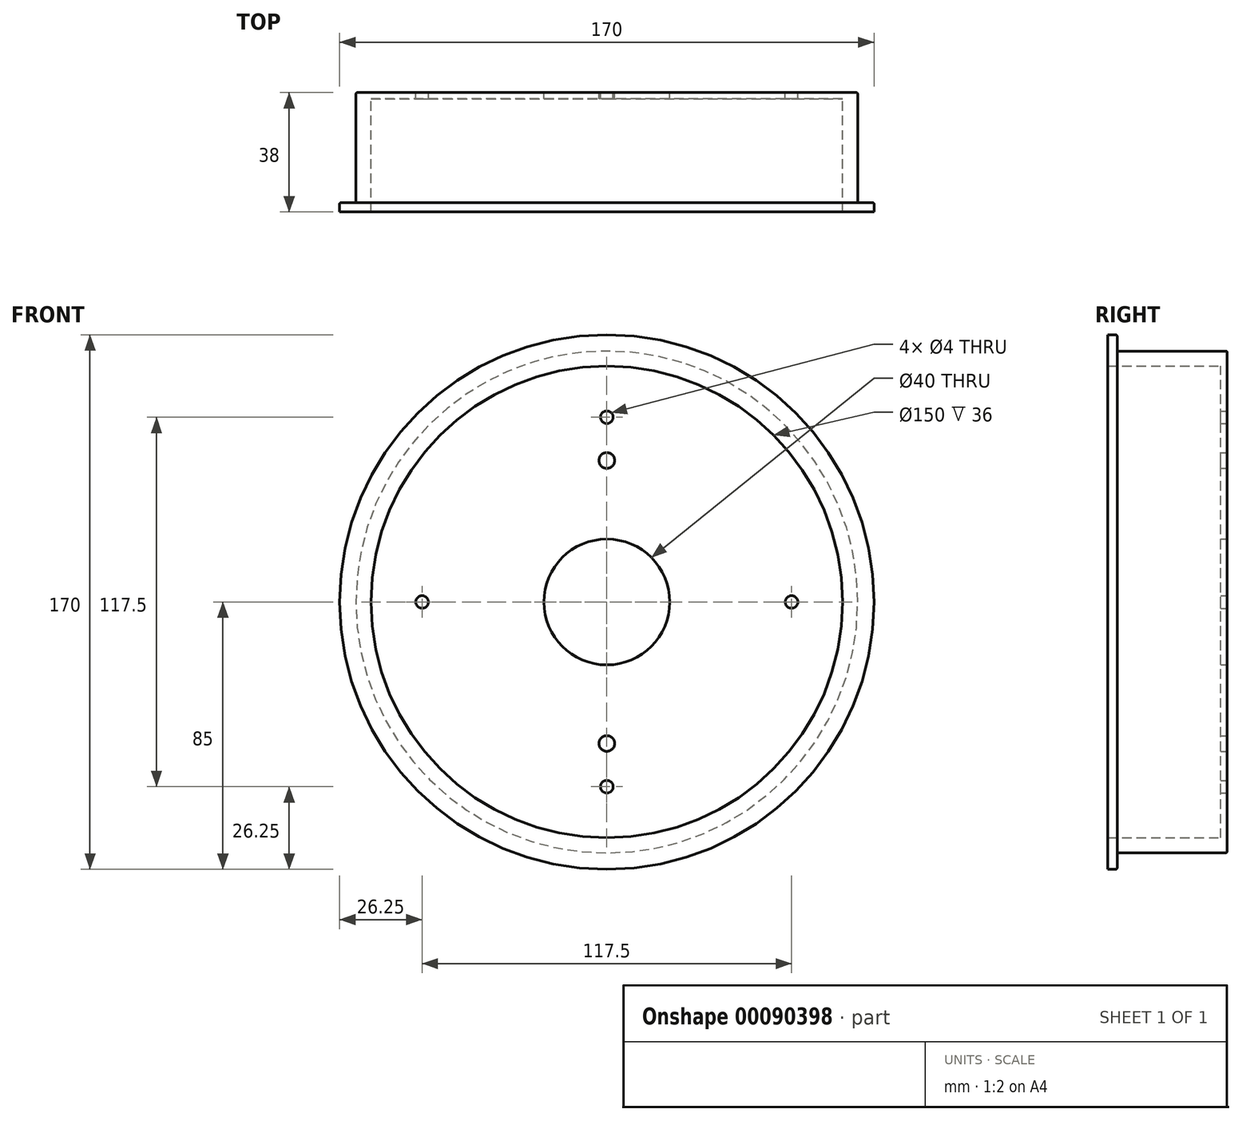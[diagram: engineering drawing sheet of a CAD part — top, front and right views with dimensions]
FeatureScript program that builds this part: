
annotation { "Feature Type Name" : "Feature", "Feature Type Description" : "" }
export const myFeature = defineFeature(function(context is Context, id is Id, definition is map)
    precondition{}
    {
        {
            var Q0;
            Q0=qCreatedBy(makeId("Front.planeOp"),FACE);
            var sketch = newSketch(context, id + "F0", { "sketchPlane" : qUnion([Q0])});
            skCircle(sketch, "E0", {"center": v(0, 0) * mm, "radius": 79.8 * mm});
            skCircle(sketch, "E1", {"center": v(0, 0) * mm, "radius": 20 * mm});
            skSolve(sketch);
        }
        {
            var Q0;
            Q0 = qSketchRegion(id + "F0", true);
            extrude(context, id + "F1", {"entities" : qUnion([Q0]), "depth" : 5 * mm});
        }
        {
            var Q0;
            Q0=makeQuery(id+"F1.opExtrude","CAP_FACE",FACE,{"disambiguationData":[OSD([sQuery(id+"F0.wireOp",EDGE,"E0"),sQuery(id+"F0.wireOp",EDGE,"E1")])],"isStart":false});
            var sketch = newSketch(context, id + "F2", { "sketchPlane" : qUnion([Q0])});
            skCircle(sketch, "E2", {"center": v(0, 0) * mm, "radius": 79.8 * mm});
            skCircle(sketch, "E3", {"center": v(0, 0) * mm, "radius": 75 * mm});
            skSolve(sketch);
        }
        {
            var Q0;
            Q0 = qSketchRegion(id + "F2", true);
            extrude(context, id + "F3", {"entities" : qUnion([Q0]), "operationType" : NewBodyOperationType.ADD, "depth" : 30 * mm});
        }
        {
            var Q0;
            Q0=makeQuery(id+"F3.opExtrude","CAP_FACE",FACE,{"disambiguationData":[OSD([sQuery(id+"F2.wireOp",EDGE,"E2"),sQuery(id+"F2.wireOp",EDGE,"E3")])],"isStart":false});
            var sketch = newSketch(context, id + "F4", { "sketchPlane" : qUnion([Q0])});
            skCircle(sketch, "E4", {"center": v(0, 0) * mm, "radius": 75 * mm});
            skCircle(sketch, "E5", {"center": v(0, 0) * mm, "radius": 85 * mm});
            skSolve(sketch);
        }
        {
            var Q0;
            Q0 = qSketchRegion(id + "F4", true);
            extrude(context, id + "F5", {"entities" : qUnion([Q0]), "operationType" : NewBodyOperationType.ADD, "depth" : 3 * mm});
        }
        {
            var Q0;
            {var subQ0=sQuery(id+"F0.wireOp",EDGE,"E1");Q0=makeQuery(id+"Fkw0NaJdu9EZw4x_1.boolean.opBoolean","SPLIT",FACE,{"disambiguationData":[TD([makeQuery(id+"F1.opExtrude","SWEPT_FACE",FACE,{"disambiguationData":[OSD([subQ0])]})])],"derivedFrom":makeQuery(id+"F1.opExtrude","CAP_FACE",FACE,{"disambiguationData":[OSD([sQuery(id+"F0.wireOp",EDGE,"E0"),subQ0])],"isStart":true})});}
            var sketch = newSketch(context, id + "F6", { "sketchPlane" : qUnion([Q0])});
            skCircle(sketch, "E6", {"center": v(0, 0) * mm, "radius": 45 * mm});
            skPoint(sketch, "E7", {"position": v(0, 45) * mm});
            skPoint(sketch, "E8", {"position": v(0, -45) * mm});
            skSolve(sketch);
        }
        {
            var Q0;
            Q0=sQuery(id+"F6.wireOp",VERTEX,"E7");
            var Q1;
            Q1=sQuery(id+"F6.wireOp",VERTEX,"E8");
            var Q2;
            Q2=makeQuery(id+"F1.opExtrude","SWEPT_BODY",BODY,{"disambiguationData":[OSD([sQuery(id+"F0.wireOp",EDGE,"E0"),sQuery(id+"F0.wireOp",EDGE,"E1")])]});
            hole(context, id + "F7", {"style" : HoleStyle.SIMPLE, "endStyle" : HoleEndStyle.BLIND, "holeDiameter" : 5 * mm, "holeDepth" : 25 * mm, "startFromSketch" : true, "locations" : qUnion([Q0, Q1]), "scope" : qUnion([Q2])});
        }
        {
            var Q0;
            Q0=makeQuery(id+"Fkw0NaJdu9EZw4x_1.opExtrude","CAP_FACE",FACE,{"disambiguationData":[OSD([sQuery(id+"FUGyWykdeStrJJa_1.wireOp",EDGE,"18ovhjpk-NtQe-Y3bV-f5br-2dgLtojzSKIQ"),sQuery(id+"FUGyWykdeStrJJa_1.wireOp",EDGE,"Cdf01vxO-JlfB-BUwl-xnIF-D1IGmlszCuzn")])],"isStart":false});
            var Q1;
            Q1=makeQuery(id+"F1.opExtrude","CAP_EDGE",EDGE,{"disambiguationData":[OSD([sQuery(id+"F0.wireOp",EDGE,"E0")])],"isStart":true});
            var Q2;
            Q2=makeQuery(id+"F5.opExtrude","CAP_EDGE",EDGE,{"disambiguationData":[OSD([sQuery(id+"F4.wireOp",EDGE,"E5")])],"isStart":true});
            fillet(context, id + "F8", {"entities" : qUnion([Q0, Q1, Q2]), "radius" : 0.5 * mm, "tangentPropagation" : true, "allowEdgeOverflow" : false});
        }
        {
            var Q0;
            Q0=makeQuery(id+"F1.opExtrude","CAP_FACE",FACE,{"disambiguationData":[OSD([sQuery(id+"F0.wireOp",EDGE,"E0"),sQuery(id+"F0.wireOp",EDGE,"E1")])],"isStart":false});
            extrude(context, id + "F9", {"entities" : qUnion([Q0]), "operationType" : NewBodyOperationType.REMOVE, "oppositeDirection" : true, "depth" : 3 * mm});
        }
        {
            var Q0;
            Q0=makeQuery(id+"F1.opExtrude","CAP_FACE",FACE,{"disambiguationData":[OSD([sQuery(id+"F0.wireOp",EDGE,"E0"),sQuery(id+"F0.wireOp",EDGE,"E1")])],"isStart":true});
            var sketch = newSketch(context, id + "F10", { "sketchPlane" : qUnion([Q0])});
            skCircle(sketch, "E9", {"center": v(0, 0) * mm, "radius": 58.75 * mm});
            skPoint(sketch, "E10", {"position": v(-58.75, 0) * mm});
            skPoint(sketch, "E11", {"position": v(0, 58.75) * mm});
            skPoint(sketch, "E12", {"position": v(58.75, 0) * mm});
            skPoint(sketch, "E13", {"position": v(0, -58.75) * mm});
            skSolve(sketch);
        }
        {
            var Q0;
            Q0=sQuery(id+"F10.wireOp",VERTEX,"E10");
            var Q1;
            Q1=sQuery(id+"F10.wireOp",VERTEX,"E11");
            var Q2;
            Q2=sQuery(id+"F10.wireOp",VERTEX,"E12");
            var Q3;
            Q3=sQuery(id+"F10.wireOp",VERTEX,"E13");
            var Q4;
            Q4=makeQuery(id+"F1.opExtrude","SWEPT_BODY",BODY,{"disambiguationData":[OSD([sQuery(id+"F0.wireOp",EDGE,"E0"),sQuery(id+"F0.wireOp",EDGE,"E1")])]});
            hole(context, id + "F11", {"style" : HoleStyle.SIMPLE, "endStyle" : HoleEndStyle.BLIND, "holeDiameter" : 4 * mm, "holeDepth" : 25 * mm, "startFromSketch" : true, "locations" : qUnion([Q0, Q1, Q2, Q3]), "scope" : qUnion([Q4])});
        }
    });
